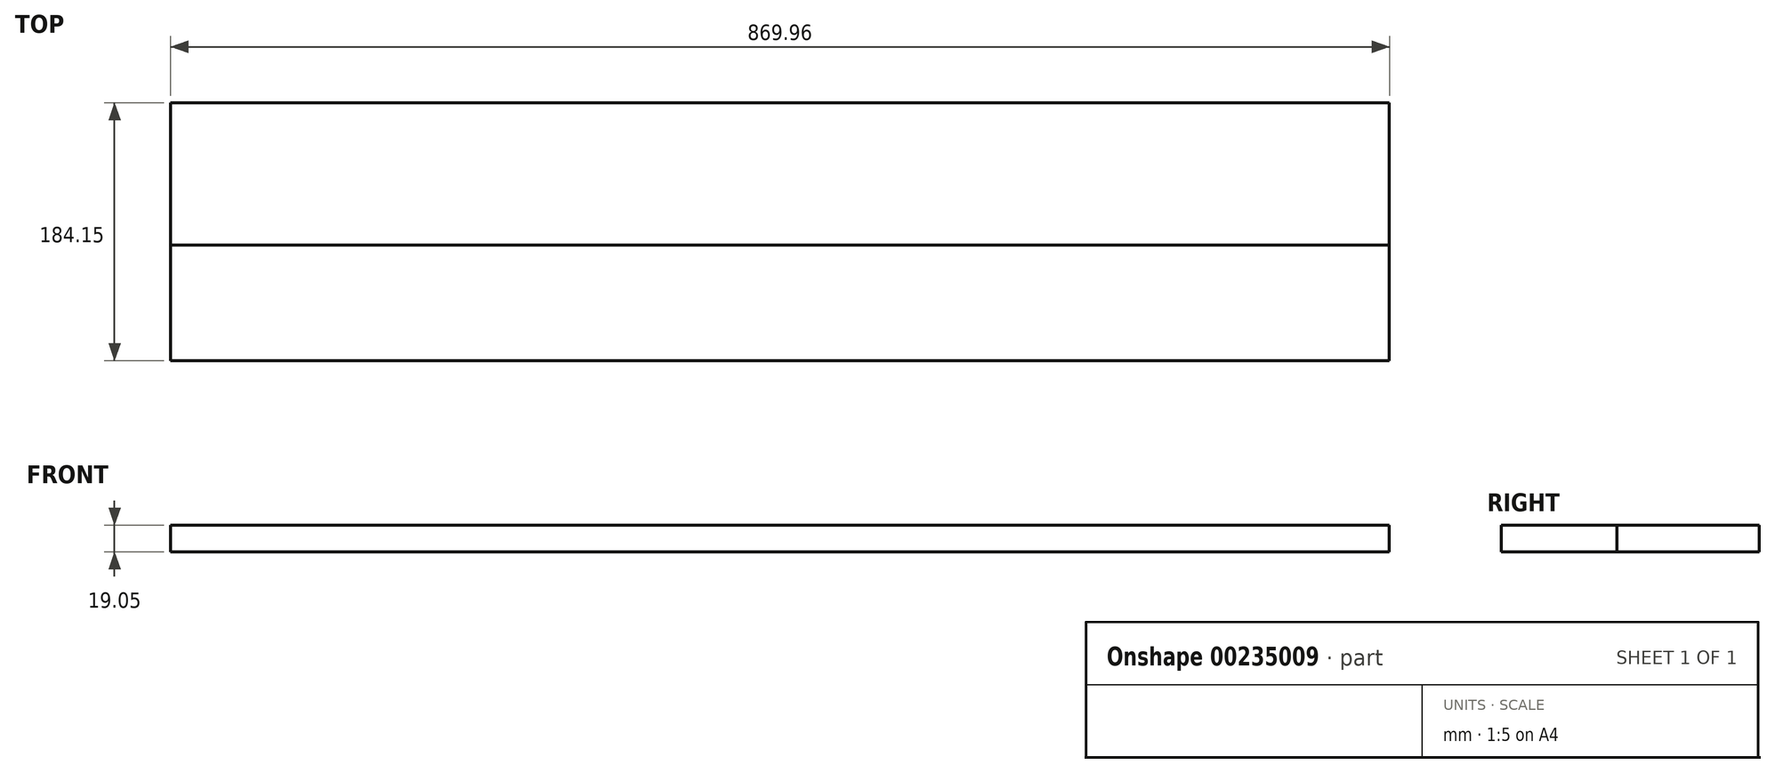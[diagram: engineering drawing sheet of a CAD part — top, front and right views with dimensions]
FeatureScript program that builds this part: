
annotation { "Feature Type Name" : "Feature", "Feature Type Description" : "" }
export const myFeature = defineFeature(function(context is Context, id is Id, definition is map)
    precondition{}
    {
        {
            var Q0;
            Q0=qCreatedBy(makeId("Top.planeOp"),FACE);
            var sketch = newSketch(context, id + "F0", { "sketchPlane" : qUnion([Q0])});
            skLineSegment(sketch, "E0.bottom", {"start": v(-434.98, 0) * mm, "end": v(434.98, 0) * mm});
            skLineSegment(sketch, "E0.top", {"start": v(-434.97, 101.6) * mm, "end": v(434.97, 101.6) * mm});
            skLineSegment(sketch, "E0.left", {"start": v(-434.98, 0) * mm, "end": v(-434.98, 101.6) * mm});
            skLineSegment(sketch, "E0.right", {"start": v(434.98, 0) * mm, "end": v(434.98, 101.6) * mm});
            skSolve(sketch);
        }
        {
            var Q0;
            Q0=makeQuery(id+"F0.imprint","IMPRINT",FACE,{"disambiguationData":[TD([[makeQuery(id+"F0.imprint","IMPRINT",EDGE,{"derivedFrom":sQuery(id+"F0.wireOp",EDGE,"E0.bottom")}),1.0]])]});
            extrude(context, id + "F1", {"entities" : qUnion([Q0]), "depth" : 19.05 * mm});
        }
        {
            var Q0;
            Q0=qCreatedBy(makeId("Top.planeOp"),FACE);
            var sketch = newSketch(context, id + "F2", { "sketchPlane" : qUnion([Q0])});
            skLineSegment(sketch, "E1.bottom", {"start": v(434.98, 0) * mm, "end": v(-434.98, 0) * mm});
            skLineSegment(sketch, "E1.top", {"start": v(434.98, -82.55) * mm, "end": v(-434.98, -82.55) * mm});
            skLineSegment(sketch, "E1.left", {"start": v(434.98, 0) * mm, "end": v(434.98, -82.55) * mm});
            skLineSegment(sketch, "E1.right", {"start": v(-434.98, 0) * mm, "end": v(-434.98, -82.55) * mm});
            skSolve(sketch);
        }
        {
            var Q0;
            Q0=makeQuery(id+"F2.imprint","IMPRINT",FACE,{"disambiguationData":[TD([[makeQuery(id+"F2.imprint","IMPRINT",EDGE,{"derivedFrom":sQuery(id+"F2.wireOp",EDGE,"E1.bottom")}),1.0]])]});
            var Q1;
            Q1=makeQuery(id+"F1.opExtrude","CAP_FACE",FACE,{"disambiguationData":[OSD([sQuery(id+"F0.wireOp",EDGE,"E0.bottom"),sQuery(id+"F0.wireOp",EDGE,"E0.top"),sQuery(id+"F0.wireOp",EDGE,"E0.left"),sQuery(id+"F0.wireOp",EDGE,"E0.right")])],"isStart":false});
            extrude(context, id + "F3", {"entities" : qUnion([Q0]), "endBound" : BoundingType.UP_TO_SURFACE, "endBoundEntityFace" : qUnion([Q1]), "depth" : 25.4 * mm});
        }
    });
